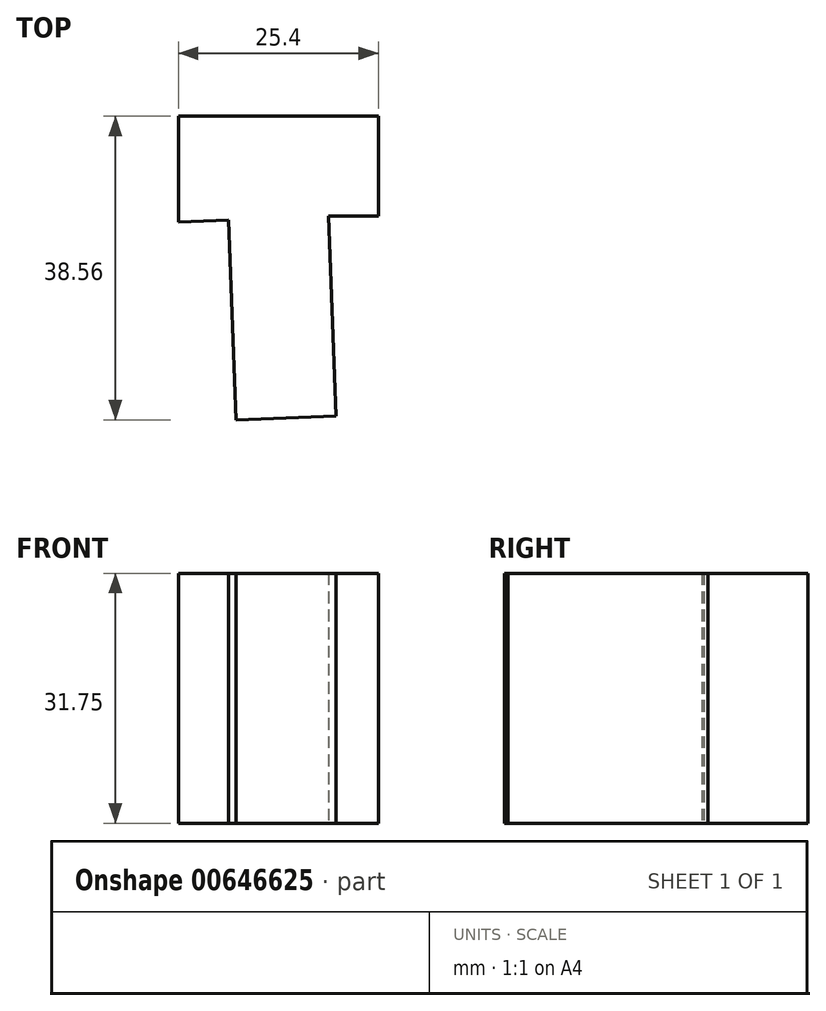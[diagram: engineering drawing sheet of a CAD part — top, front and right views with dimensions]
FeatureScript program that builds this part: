
annotation { "Feature Type Name" : "Feature", "Feature Type Description" : "" }
export const myFeature = defineFeature(function(context is Context, id is Id, definition is map)
    precondition{}
    {
        {
            var Q0;
            Q0=qCreatedBy(makeId("Top.planeOp"),FACE);
            var sketch = newSketch(context, id + "F0", { "sketchPlane" : qUnion([Q0])});
            skLineSegment(sketch, "E0", {"start": v(-20.01, 38.08) * mm, "end": v(5.39, 38.08) * mm});
            skLineSegment(sketch, "E1", {"start": v(5.39, 38.08) * mm, "end": v(5.39, 25.38) * mm});
            skLineSegment(sketch, "E2", {"start": v(5.39, 25.38) * mm, "end": v(-0.96, 25.38) * mm});
            skLineSegment(sketch, "E3", {"start": v(-0.96, 25.38) * mm, "end": v(0, 0) * mm});
            skLineSegment(sketch, "E4", {"start": v(0, 0) * mm, "end": v(-12.7, -0.48) * mm});
            skLineSegment(sketch, "E5", {"start": v(-12.7, -0.48) * mm, "end": v(-13.65, 24.9) * mm});
            skLineSegment(sketch, "E6", {"start": v(-13.65, 24.9) * mm, "end": v(-20, 24.66) * mm});
            skLineSegment(sketch, "E7", {"start": v(-20, 24.66) * mm, "end": v(-20.01, 38.08) * mm});
            skSolve(sketch);
        }
        {
            var Q0;
            Q0=makeQuery(id+"F0.imprint","IMPRINT",FACE,{"disambiguationData":[TD([[makeQuery(id+"F0.imprint","IMPRINT",EDGE,{"derivedFrom":sQuery(id+"F0.wireOp",EDGE,"E0")}),-1.0]])]});
            extrude(context, id + "F1", {"entities" : qUnion([Q0]), "depth" : 31.75 * mm, "offsetDistance" : 25.4 * mm});
        }
    });
